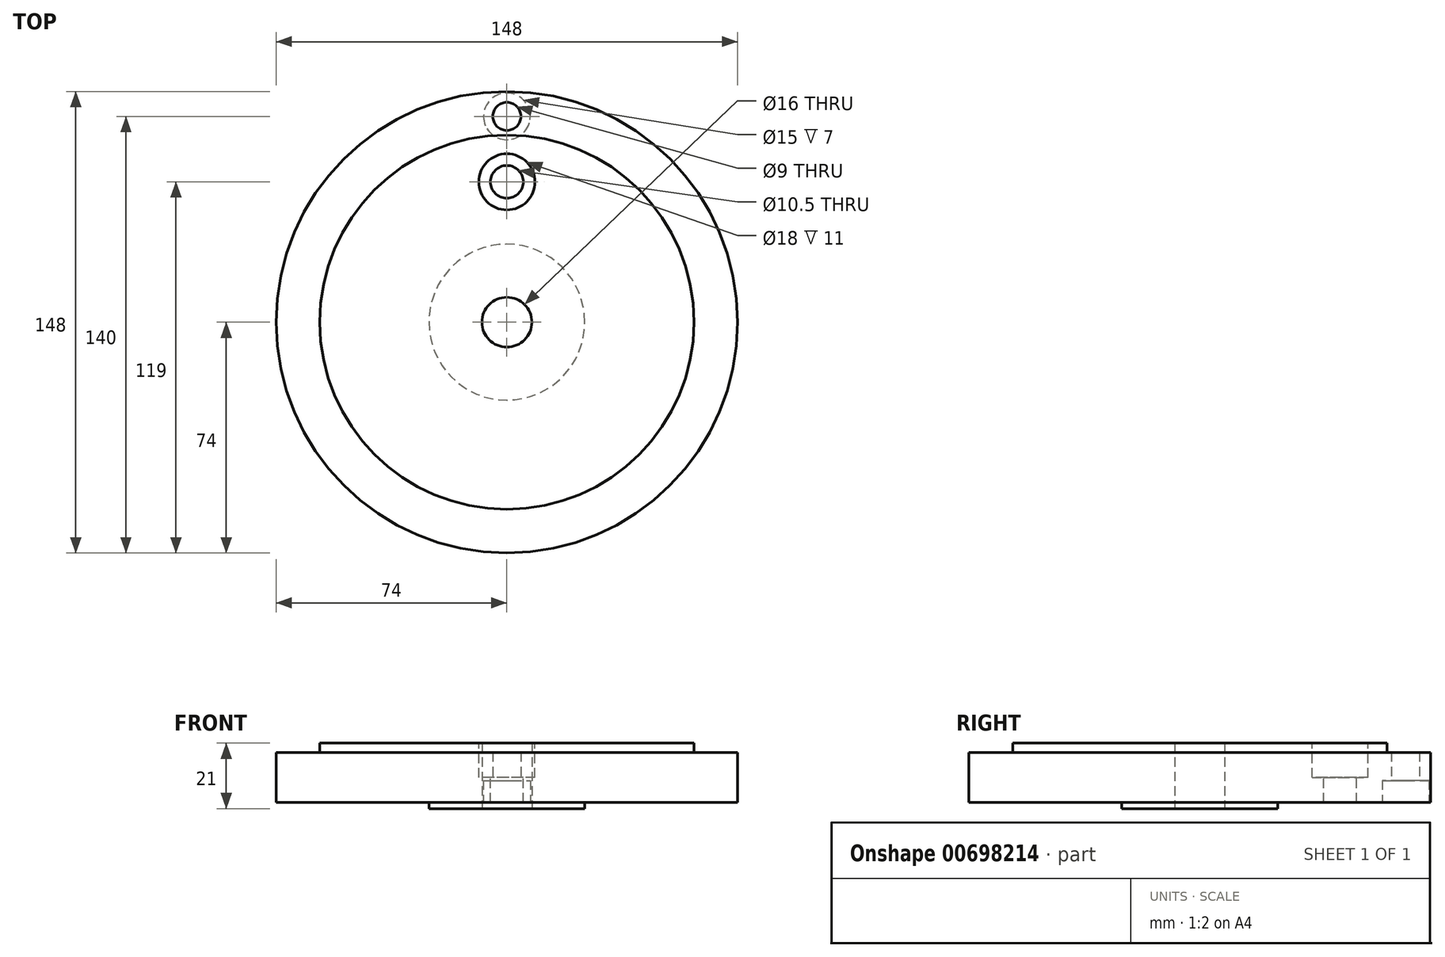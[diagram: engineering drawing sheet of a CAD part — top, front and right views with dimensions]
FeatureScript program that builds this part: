
annotation { "Feature Type Name" : "Feature", "Feature Type Description" : "" }
export const myFeature = defineFeature(function(context is Context, id is Id, definition is map)
    precondition{}
    {
        {
            var Q0;
            Q0=qCreatedBy(makeId("Top.planeOp"),FACE);
            var sketch = newSketch(context, id + "F0", { "sketchPlane" : qUnion([Q0])});
            skCircle(sketch, "E0", {"center": v(0, 0) * mm, "radius": 74 * mm});
            skSolve(sketch);
        }
        {
            var Q0;
            Q0 = qSketchRegion(id + "F0", true);
            extrude(context, id + "F1", {"entities" : qUnion([Q0]), "depth" : 16 * mm, "offsetDistance" : 25 * mm});
        }
        {
            var Q0;
            Q0=makeQuery(id+"F1.opExtrude","CAP_FACE",FACE,{"disambiguationData":[OSD([sQuery(id+"F0.wireOp",EDGE,"E0")])],"isStart":true});
            var sketch = newSketch(context, id + "F2", { "sketchPlane" : qUnion([Q0])});
            skCircle(sketch, "E1", {"center": v(0, 0) * mm, "radius": 25 * mm});
            skSolve(sketch);
        }
        {
            var Q0;
            Q0=makeQuery(id+"F2.imprint","IMPRINT",FACE,{"disambiguationData":[TD([[makeQuery(id+"F2.imprint","IMPRINT",EDGE,{"derivedFrom":sQuery(id+"F2.wireOp",EDGE,"E1")}),1.0]])]});
            extrude(context, id + "F3", {"entities" : qUnion([Q0]), "operationType" : NewBodyOperationType.ADD, "depth" : 2 * mm, "offsetDistance" : 25 * mm});
        }
        {
            var Q0;
            Q0=makeQuery(id+"F3.opExtrude","CAP_FACE",FACE,{"disambiguationData":[OSD([sQuery(id+"F2.wireOp",EDGE,"E1")])],"isStart":false});
            var sketch = newSketch(context, id + "F4", { "sketchPlane" : qUnion([Q0])});
            skPoint(sketch, "E2", {"position": v(0, 0) * mm});
            skCircle(sketch, "E3", {"center": v(0, 0) * mm, "radius": 66 * mm, "construction": true});
            skPoint(sketch, "E4", {"position": v(0, -66) * mm});
            skSolve(sketch);
        }
        {
            var Q0;
            Q0=sQuery(id+"F4.wireOp",VERTEX,"E2");
            var Q1;
            Q1=makeQuery(id+"F1.opExtrude","SWEPT_BODY",BODY,{"disambiguationData":[OSD([sQuery(id+"F0.wireOp",EDGE,"E0")])]});
            hole(context, id + "F5", {"style" : HoleStyle.SIMPLE, "endStyle" : HoleEndStyle.THROUGH, "holeDiameter" : 16 * mm, "majorDiameter" : 5 * mm, "isTappedThrough" : true, "tappedDepth" : 12 * mm, "tapClearance" : 3, "startFromSketch" : true, "locations" : qUnion([Q0]), "scope" : qUnion([Q1])});
        }
        {
            var Q0;
            Q0=sQuery(id+"F4.wireOp",VERTEX,"E4");
            var Q1;
            Q1=makeQuery(id+"F1.opExtrude","SWEPT_BODY",BODY,{"disambiguationData":[OSD([sQuery(id+"F0.wireOp",EDGE,"E0")])]});
            hole(context, id + "F6", {"style" : HoleStyle.C_BORE, "endStyle" : HoleEndStyle.THROUGH, "holeDiameter" : 9 * mm, "cBoreDiameter" : 15 * mm, "cBoreDepth" : 9 * mm, "majorDiameter" : 5 * mm, "isTappedThrough" : true, "tappedDepth" : 12 * mm, "tapClearance" : 3, "startFromSketch" : true, "locations" : qUnion([Q0]), "scope" : qUnion([Q1])});
        }
        {
            var Q0;
            Q0=makeQuery(id+"F1.opExtrude","CAP_FACE",FACE,{"disambiguationData":[OSD([sQuery(id+"F0.wireOp",EDGE,"E0")])],"isStart":false});
            var sketch = newSketch(context, id + "F7", { "sketchPlane" : qUnion([Q0])});
            skCircle(sketch, "E5", {"center": v(0, 0) * mm, "radius": 60 * mm});
            skSolve(sketch);
        }
        {
            var Q0;
            Q0=makeQuery(id+"F7.imprint","IMPRINT",FACE,{"disambiguationData":[TD([[makeQuery(id+"F7.imprint","IMPRINT",EDGE,{"derivedFrom":sQuery(id+"F7.wireOp",EDGE,"E5")}),1.0]])]});
            extrude(context, id + "F8", {"entities" : qUnion([Q0]), "operationType" : NewBodyOperationType.ADD, "depth" : 3 * mm, "offsetDistance" : 25 * mm});
        }
        {
            var Q0;
            Q0=makeQuery(id+"F8.opExtrude","CAP_FACE",FACE,{"disambiguationData":[OSD([sQuery(id+"F0.wireOp",EDGE,"E0"),sQuery(id+"F5.hole-0.sketch.wireOp",EDGE,"core_line_2"),sQuery(id+"F7.wireOp",EDGE,"E5")])],"isStart":false});
            var sketch = newSketch(context, id + "F9", { "sketchPlane" : qUnion([Q0])});
            skCircle(sketch, "E6", {"center": v(0, 0) * mm, "radius": 45 * mm, "construction": true});
            skPoint(sketch, "E7", {"position": v(0, 45) * mm});
            skSolve(sketch);
        }
        {
            var Q0;
            Q0=sQuery(id+"F9.wireOp",VERTEX,"E7");
            var Q1;
            Q1=makeQuery(id+"F1.opExtrude","SWEPT_BODY",BODY,{"disambiguationData":[OSD([sQuery(id+"F0.wireOp",EDGE,"E0")])]});
            hole(context, id + "F10", {"style" : HoleStyle.C_BORE, "endStyle" : HoleEndStyle.THROUGH, "holeDiameter" : 10.5 * mm, "cBoreDiameter" : 18 * mm, "cBoreDepth" : 11 * mm, "majorDiameter" : 5 * mm, "isTappedThrough" : true, "tappedDepth" : 12 * mm, "tapClearance" : 3, "startFromSketch" : true, "locations" : qUnion([Q0]), "scope" : qUnion([Q1])});
        }
    });
